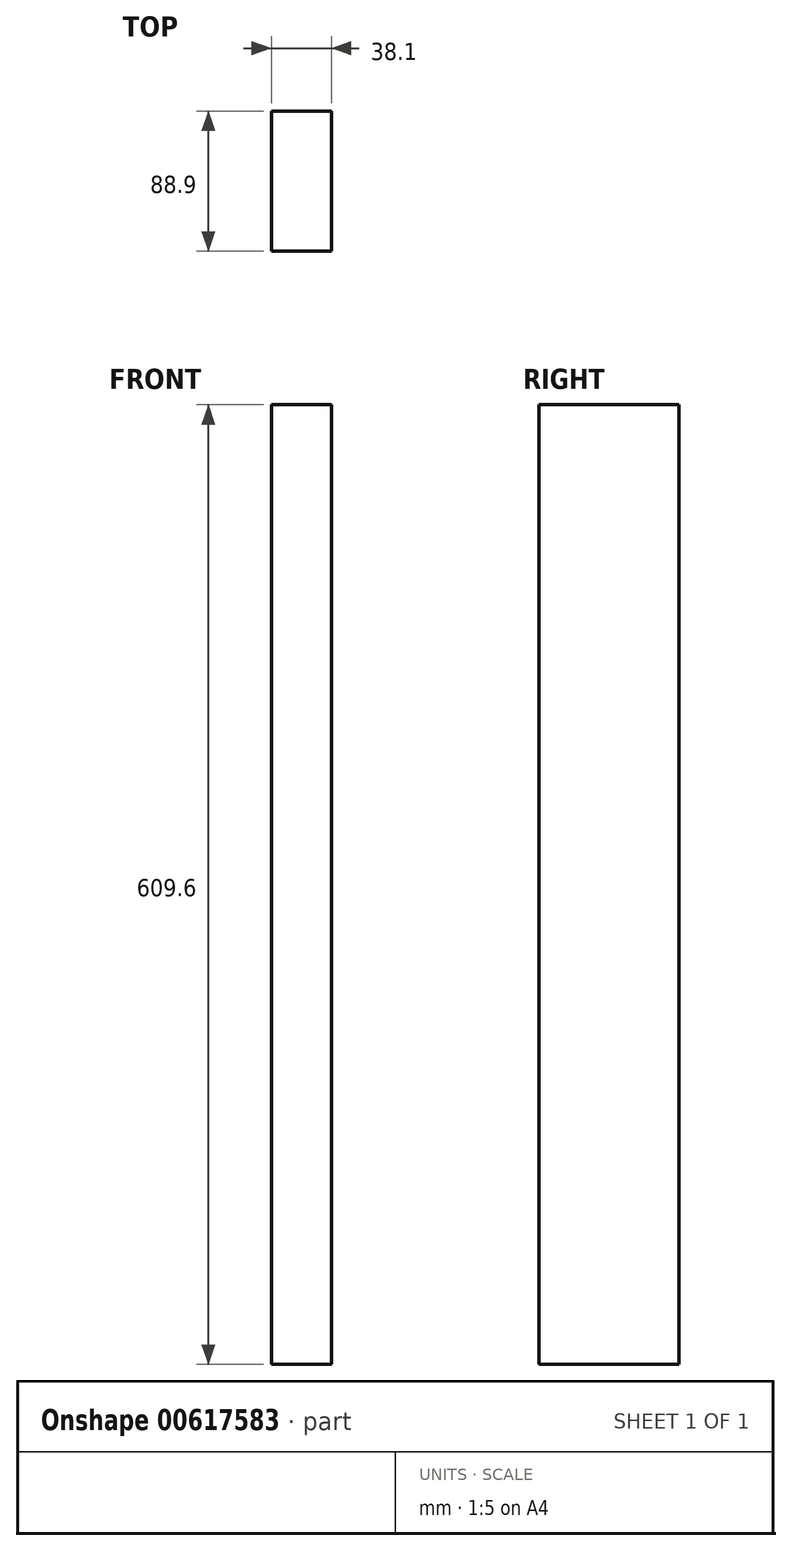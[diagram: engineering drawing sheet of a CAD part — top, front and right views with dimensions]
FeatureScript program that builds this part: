
annotation { "Feature Type Name" : "Feature", "Feature Type Description" : "" }
export const myFeature = defineFeature(function(context is Context, id is Id, definition is map)
    precondition{}
    {
        {
            var Q0;
            Q0=qCreatedBy(makeId("Front.planeOp"),FACE);
            var sketch = newSketch(context, id + "F0", { "sketchPlane" : qUnion([Q0])});
            skLineSegment(sketch, "E0.bottom", {"start": v(0, 0) * mm, "end": v(38.1, 0) * mm});
            skLineSegment(sketch, "E0.top", {"start": v(0, 609.6) * mm, "end": v(38.1, 609.6) * mm});
            skLineSegment(sketch, "E0.left", {"start": v(0, 0) * mm, "end": v(0, 609.6) * mm});
            skLineSegment(sketch, "E0.right", {"start": v(38.1, 0) * mm, "end": v(38.1, 609.6) * mm});
            skSolve(sketch);
        }
        {
            var Q0;
            Q0 = qSketchRegion(id + "F0", true);
            extrude(context, id + "F1", {"entities" : qUnion([Q0]), "endBound" : BoundingType.SYMMETRIC, "depth" : 88.9 * mm, "offsetDistance" : 25.4 * mm});
        }
    });
